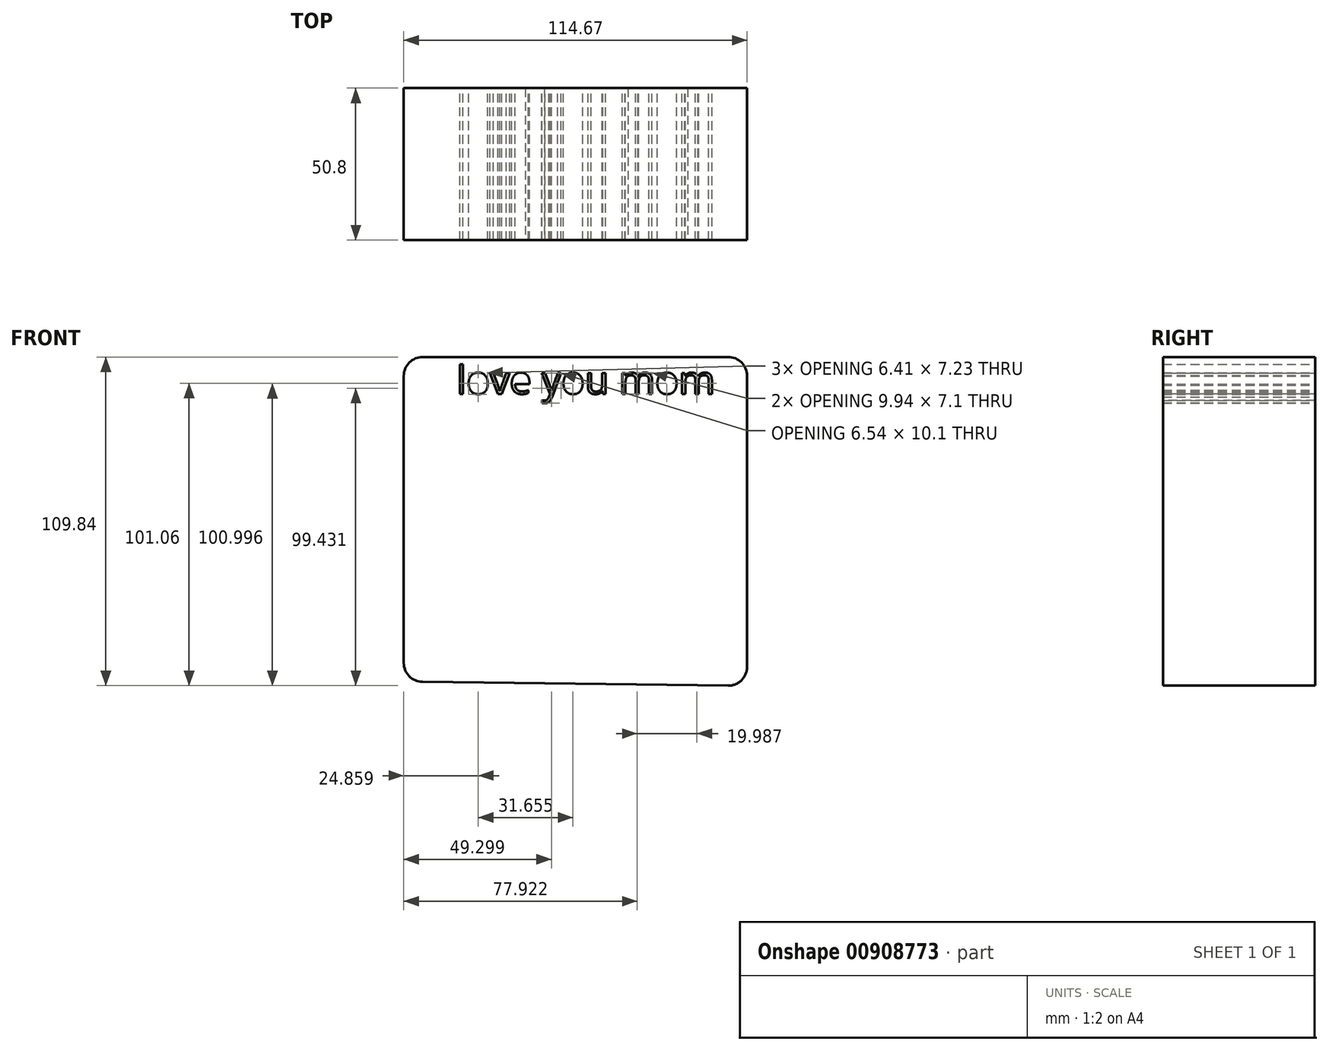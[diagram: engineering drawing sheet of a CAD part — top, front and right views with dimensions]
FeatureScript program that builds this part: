
annotation { "Feature Type Name" : "Feature", "Feature Type Description" : "" }
export const myFeature = defineFeature(function(context is Context, id is Id, definition is map)
    precondition{}
    {
        {
            var Q0;
            Q0=qCreatedBy(makeId("Front.planeOp"),FACE);
            var sketch = newSketch(context, id + "F0", { "sketchPlane" : qUnion([Q0])});
            skLineSegment(sketch, "E0", {"start": v(48.31, 53.63) * mm, "end": v(-53.66, 53.63) * mm});
            skLineSegment(sketch, "E1", {"start": v(-60.01, 47.28) * mm, "end": v(-60.01, -48.6) * mm});
            skLineSegment(sketch, "E2", {"start": v(54.66, 47.28) * mm, "end": v(54.66, -49.86) * mm});
            skLineSegment(sketch, "E3", {"start": v(48.23, -56.2) * mm, "end": v(-53.74, -54.94) * mm});
            skLineSegment(sketch, "E4", {"start": v(-56.82, -39.27) * mm, "end": v(-56.82, -41) * mm});
            skLineSegment(sketch, "E5", {"start": v(-58.81, -47.25) * mm, "end": v(-58.81, -49.37) * mm});
            skLineSegment(sketch, "E6", {"start": v(-58.81, -49.37) * mm, "end": v(-56.82, -49.37) * mm});
            skLineSegment(sketch, "E7", {"start": v(-56.82, -49.37) * mm, "end": v(-56.82, -47.25) * mm});
            skLineSegment(sketch, "E8", {"start": v(-54.03, -47.25) * mm, "end": v(-54.03, -49.37) * mm});
            skLineSegment(sketch, "E9", {"start": v(-44.32, -49.37) * mm, "end": v(-44.32, -47.25) * mm});
            skLineSegment(sketch, "E10", {"start": v(-40.74, -47.25) * mm, "end": v(-40.74, -49.37) * mm});
            skLineSegment(sketch, "E11", {"start": v(-36.22, -41) * mm, "end": v(-36.22, -39.27) * mm});
            skLineSegment(sketch, "E12", {"start": v(-35.02, -41) * mm, "end": v(-33.56, -41) * mm});
            skText(sketch, "E13", { "text": "love you mom\n", "fontName": "OpenSans-Regular.ttf"});
            skPoint(sketch, "E14.visualSharp", {"position": v(-60.01, 53.63) * mm});
            skArc(sketch, "E14.filletArc", {"start": v(-53.66, 53.63) * mm, "mid": v(-58.15, 51.77) * mm, "end": v(-60.01, 47.28) * mm});
            skPoint(sketch, "E15.visualSharp", {"position": v(-60.01, -54.87) * mm});
            skArc(sketch, "E15.filletArc", {"start": v(-60.01, -48.6) * mm, "mid": v(-58.18, -53.06) * mm, "end": v(-53.74, -54.94) * mm});
            skPoint(sketch, "E16.visualSharp", {"position": v(54.66, -56.29) * mm});
            skArc(sketch, "E16.filletArc", {"start": v(48.23, -56.2) * mm, "mid": v(52.77, -54.37) * mm, "end": v(54.66, -49.86) * mm});
            skPoint(sketch, "E17.visualSharp", {"position": v(54.66, 53.63) * mm});
            skArc(sketch, "E17.filletArc", {"start": v(54.66, 47.28) * mm, "mid": v(52.8, 51.77) * mm, "end": v(48.31, 53.63) * mm});
            const initialGuessF0  = {"E13": [-0.04238, 0.0413, 1, 0, 0.00938]};
            skSetInitialGuess(sketch, initialGuessF0);
            skSolve(sketch);
        }
        {
            var Q0;
            Q0 = qSketchRegion(id + "F0", true);
            extrude(context, id + "F1", {"entities" : qUnion([Q0]), "endBound" : BoundingType.SYMMETRIC, "depth" : 50.8 * mm, "offsetDistance" : 25.4 * mm});
        }
    });
